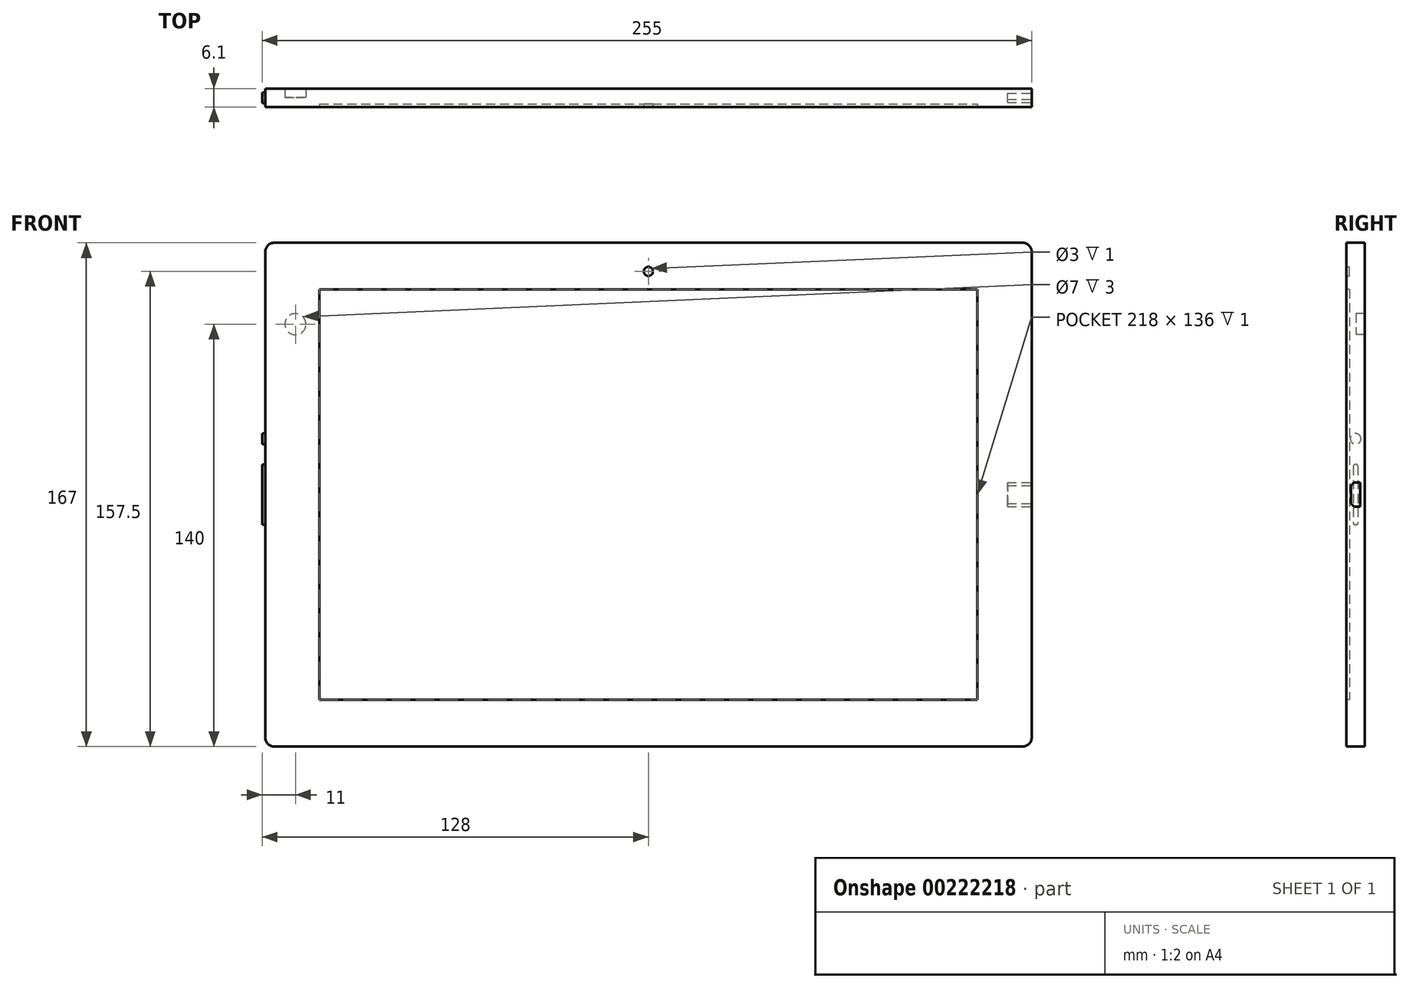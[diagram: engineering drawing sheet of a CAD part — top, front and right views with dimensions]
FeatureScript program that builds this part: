
annotation { "Feature Type Name" : "Feature", "Feature Type Description" : "" }
export const myFeature = defineFeature(function(context is Context, id is Id, definition is map)
    precondition{}
    {
        {
            var Q0;
            Q0=qCreatedBy(makeId("Front.planeOp"),FACE);
            var sketch = newSketch(context, id + "F0", { "sketchPlane" : qUnion([Q0])});
            skLineSegment(sketch, "E0.bottom", {"start": v(-127, 83.5) * mm, "end": v(127, 83.5) * mm});
            skLineSegment(sketch, "E0.top", {"start": v(-127, -83.5) * mm, "end": v(127, -83.5) * mm});
            skLineSegment(sketch, "E0.left", {"start": v(-127, 83.5) * mm, "end": v(-127, -83.5) * mm});
            skLineSegment(sketch, "E0.right", {"start": v(127, 83.5) * mm, "end": v(127, -83.5) * mm});
            skPoint(sketch, "E1", {"position": v(0, 83.5) * mm});
            skPoint(sketch, "E2", {"position": v(127, 0) * mm});
            skSolve(sketch);
        }
        {
            var Q0;
            Q0=makeQuery(id+"F0.imprint","IMPRINT",FACE,{"disambiguationData":[TD([[makeQuery(id+"F0.imprint","IMPRINT",EDGE,{"derivedFrom":sQuery(id+"F0.wireOp",EDGE,"E0.bottom")}),-1.0]])]});
            extrude(context, id + "F1", {"entities" : qUnion([Q0]), "endBound" : BoundingType.SYMMETRIC, "depth" : 6.1 * mm});
        }
        {
            var Q0;
            Q0=makeQuery(id+"F1.opExtrude","SWEPT_EDGE",EDGE,{"disambiguationData":[OSD([sQuery(id+"F0.wireOp",EDGE,"E0.bottom"),sQuery(id+"F0.wireOp",EDGE,"E0.right")])]});
            var Q1;
            Q1=makeQuery(id+"F1.opExtrude","SWEPT_EDGE",EDGE,{"disambiguationData":[OSD([sQuery(id+"F0.wireOp",EDGE,"E0.top"),sQuery(id+"F0.wireOp",EDGE,"E0.right")])]});
            var Q2;
            Q2=makeQuery(id+"F1.opExtrude","SWEPT_EDGE",EDGE,{"disambiguationData":[OSD([sQuery(id+"F0.wireOp",EDGE,"E0.top"),sQuery(id+"F0.wireOp",EDGE,"E0.left")])]});
            var Q3;
            Q3=makeQuery(id+"F1.opExtrude","SWEPT_EDGE",EDGE,{"disambiguationData":[OSD([sQuery(id+"F0.wireOp",EDGE,"E0.bottom"),sQuery(id+"F0.wireOp",EDGE,"E0.left")])]});
            fillet(context, id + "F2", {"entities" : qUnion([Q0, Q1, Q2, Q3]), "radius" : 3 * mm, "tangentPropagation" : true, "allowEdgeOverflow" : false});
        }
        {
            var Q0;
            Q0=makeQuery(id+"F1.opExtrude","CAP_FACE",FACE,{"disambiguationData":[OSD([sQuery(id+"F0.wireOp",EDGE,"E0.bottom"),sQuery(id+"F0.wireOp",EDGE,"E0.top"),sQuery(id+"F0.wireOp",EDGE,"E0.left"),sQuery(id+"F0.wireOp",EDGE,"E0.right")])],"isStart":false});
            var sketch = newSketch(context, id + "F3", { "sketchPlane" : qUnion([Q0])});
            skLineSegment(sketch, "E3.bottom", {"start": v(-109, 68) * mm, "end": v(109, 68) * mm});
            skLineSegment(sketch, "E3.top", {"start": v(-109, -68) * mm, "end": v(109, -68) * mm});
            skLineSegment(sketch, "E3.left", {"start": v(-109, 68) * mm, "end": v(-109, -68) * mm});
            skLineSegment(sketch, "E3.right", {"start": v(109, 68) * mm, "end": v(109, -68) * mm});
            skPoint(sketch, "E4", {"position": v(0, 68) * mm});
            skPoint(sketch, "E5", {"position": v(-109, 0) * mm});
            skPoint(sketch, "E6", {"position": v(0, 83.5) * mm});
            skPoint(sketch, "E7", {"position": v(-127, 0) * mm});
            skCircle(sketch, "E8", {"center": v(0, 74) * mm, "radius": 1.5 * mm});
            skSolve(sketch);
        }
        {
            var Q0;
            Q0=makeQuery(id+"F3.imprint","IMPRINT",FACE,{"disambiguationData":[TD([[makeQuery(id+"F3.imprint","IMPRINT",EDGE,{"derivedFrom":sQuery(id+"F3.wireOp",EDGE,"E3.bottom")}),-1.0]])]});
            var Q1;
            Q1=makeQuery(id+"F3.imprint","IMPRINT",FACE,{"disambiguationData":[TD([[makeQuery(id+"F3.imprint","IMPRINT",EDGE,{"derivedFrom":sQuery(id+"F3.wireOp",EDGE,"E8")}),1.0]])]});
            extrude(context, id + "F4", {"entities" : qUnion([Q0, Q1]), "operationType" : NewBodyOperationType.REMOVE, "oppositeDirection" : true, "depth" : 1 * mm});
        }
        {
            var Q0;
            Q0=makeQuery(id+"F4.boolean.opBoolean","COPY",FACE,{"derivedFrom":makeQuery(id+"F4.opExtrude","CAP_FACE",FACE,{"disambiguationData":[OSD([sQuery(id+"F3.wireOp",EDGE,"E3.bottom"),sQuery(id+"F3.wireOp",EDGE,"E3.top"),sQuery(id+"F3.wireOp",EDGE,"E3.left"),sQuery(id+"F3.wireOp",EDGE,"E3.right")])],"isStart":false})});
            var sketch = newSketch(context, id + "F5", { "sketchPlane" : qUnion([Q0])});
            skLineSegment(sketch, "E9.bottom", {"start": v(-109, 68) * mm, "end": v(109, 68) * mm});
            skLineSegment(sketch, "E9.top", {"start": v(-109, -68) * mm, "end": v(109, -68) * mm});
            skLineSegment(sketch, "E9.left", {"start": v(-109, 68) * mm, "end": v(-109, -68) * mm});
            skLineSegment(sketch, "E9.right", {"start": v(109, 68) * mm, "end": v(109, -68) * mm});
            skCircle(sketch, "E10.0.0", {"center": v(0, 74) * mm, "radius": 1.5 * mm});
            skSolve(sketch);
        }
        {
            var Q0;
            Q0=makeQuery(id+"F5.imprint","IMPRINT",FACE,{"disambiguationData":[TD([[makeQuery(id+"F5.imprint","IMPRINT",EDGE,{"derivedFrom":sQuery(id+"F5.wireOp",EDGE,"E9.bottom")}),-1.0]])]});
            var Q1;
            Q1=makeQuery(id+"F5.imprint","IMPRINT",FACE,{"disambiguationData":[TD([[makeQuery(id+"F5.imprint","IMPRINT",EDGE,{"derivedFrom":sQuery(id+"F5.wireOp",EDGE,"E10.0.0")}),1.0]])]});
            var Q2;
            Q2=makeQuery(id+"F1.opExtrude","CAP_FACE",FACE,{"disambiguationData":[OSD([sQuery(id+"F0.wireOp",EDGE,"E0.bottom"),sQuery(id+"F0.wireOp",EDGE,"E0.top"),sQuery(id+"F0.wireOp",EDGE,"E0.left"),sQuery(id+"F0.wireOp",EDGE,"E0.right")])],"isStart":false});
            extrude(context, id + "F6", {"entities" : qUnion([Q0, Q1]), "endBound" : BoundingType.UP_TO_SURFACE, "endBoundEntityFace" : qUnion([Q2]), "depth" : 25 * mm});
        }
        {
            var Q0;
            Q0=makeQuery(id+"F1.opExtrude","CAP_FACE",FACE,{"disambiguationData":[OSD([sQuery(id+"F0.wireOp",EDGE,"E0.bottom"),sQuery(id+"F0.wireOp",EDGE,"E0.top"),sQuery(id+"F0.wireOp",EDGE,"E0.left"),sQuery(id+"F0.wireOp",EDGE,"E0.right")])],"isStart":true});
            var sketch = newSketch(context, id + "F7", { "sketchPlane" : qUnion([Q0])});
            skCircle(sketch, "E11", {"center": v(117, 56.5) * mm, "radius": 3.5 * mm});
            skSolve(sketch);
        }
        {
            var Q0;
            Q0=makeQuery(id+"F7.imprint","IMPRINT",FACE,{"disambiguationData":[TD([[makeQuery(id+"F7.imprint","IMPRINT",EDGE,{"derivedFrom":sQuery(id+"F7.wireOp",EDGE,"E11")}),1.0]])]});
            extrude(context, id + "F8", {"entities" : qUnion([Q0]), "operationType" : NewBodyOperationType.REMOVE, "oppositeDirection" : true, "depth" : 3 * mm});
        }
        {
            var Q0;
            Q0=makeQuery(id+"F8.boolean.opBoolean","COPY",FACE,{"derivedFrom":makeQuery(id+"F8.opExtrude","CAP_FACE",FACE,{"disambiguationData":[OSD([sQuery(id+"F7.wireOp",EDGE,"E11")])],"isStart":false})});
            var sketch = newSketch(context, id + "F9", { "sketchPlane" : qUnion([Q0])});
            skCircle(sketch, "E12", {"center": v(117, 56.5) * mm, "radius": 3.5 * mm});
            skSolve(sketch);
        }
        {
            var Q0;
            Q0=makeQuery(id+"F9.imprint","IMPRINT",FACE,{"disambiguationData":[TD([[makeQuery(id+"F9.imprint","IMPRINT",EDGE,{"derivedFrom":sQuery(id+"F9.wireOp",EDGE,"E12")}),1.0]])]});
            extrude(context, id + "F10", {"entities" : qUnion([Q0]), "depth" : 3 * mm});
        }
        {
            var Q0;
            Q0=makeQuery(id+"F1.opExtrude","SWEPT_FACE",FACE,{"disambiguationData":[OSD([sQuery(id+"F0.wireOp",EDGE,"E0.left")])]});
            var sketch = newSketch(context, id + "F11", { "sketchPlane" : qUnion([Q0])});
            skCircle(sketch, "E13", {"center": v(0, 18.5) * mm, "radius": 1.75 * mm});
            skLineSegment(sketch, "E14.bottom", {"start": v(-0.15, 10) * mm, "end": v(0.15, 10) * mm});
            skLineSegment(sketch, "E14.top", {"start": v(-0.15, -10) * mm, "end": v(0.15, -10) * mm});
            skLineSegment(sketch, "E14.left", {"start": v(-0.75, 9.4) * mm, "end": v(-0.75, -9.4) * mm});
            skLineSegment(sketch, "E14.right", {"start": v(0.75, 9.4) * mm, "end": v(0.75, -9.4) * mm});
            skPoint(sketch, "E15", {"position": v(0, 10) * mm});
            skPoint(sketch, "E16", {"position": v(-0.75, 0) * mm});
            skPoint(sketch, "E17.visualSharp", {"position": v(-0.75, 10) * mm});
            skArc(sketch, "E17.filletArc", {"start": v(-0.15, 10) * mm, "mid": v(-0.57, 9.82) * mm, "end": v(-0.75, 9.4) * mm});
            skPoint(sketch, "E18.visualSharp", {"position": v(0.75, 10) * mm});
            skArc(sketch, "E18.filletArc", {"start": v(0.75, 9.4) * mm, "mid": v(0.57, 9.82) * mm, "end": v(0.15, 10) * mm});
            skPoint(sketch, "E19.visualSharp", {"position": v(0.75, -10) * mm});
            skArc(sketch, "E19.filletArc", {"start": v(0.15, -10) * mm, "mid": v(0.57, -9.82) * mm, "end": v(0.75, -9.4) * mm});
            skPoint(sketch, "E20.visualSharp", {"position": v(-0.75, -10) * mm});
            skArc(sketch, "E20.filletArc", {"start": v(-0.75, -9.4) * mm, "mid": v(-0.57, -9.82) * mm, "end": v(-0.15, -10) * mm});
            skSolve(sketch);
        }
        {
            var Q0;
            Q0=makeQuery(id+"F11.imprint","IMPRINT",FACE,{"disambiguationData":[TD([[makeQuery(id+"F11.imprint","IMPRINT",EDGE,{"derivedFrom":sQuery(id+"F11.wireOp",EDGE,"E13")}),1.0]])]});
            var Q1;
            Q1=makeQuery(id+"F11.imprint","IMPRINT",FACE,{"disambiguationData":[TD([[makeQuery(id+"F11.imprint","IMPRINT",EDGE,{"derivedFrom":sQuery(id+"F11.wireOp",EDGE,"E14.bottom")}),-1.0]])]});
            extrude(context, id + "F12", {"entities" : qUnion([Q0, Q1]), "operationType" : NewBodyOperationType.ADD, "depth" : 1 * mm});
        }
        {
            var Q0;
            Q0=makeQuery(id+"F1.opExtrude","SWEPT_FACE",FACE,{"disambiguationData":[OSD([sQuery(id+"F0.wireOp",EDGE,"E0.right")])]});
            var sketch = newSketch(context, id + "F13", { "sketchPlane" : qUnion([Q0])});
            skLineSegment(sketch, "E21", {"start": v(1.5, 4) * mm, "end": v(1.5, -4) * mm});
            skLineSegment(sketch, "E22", {"start": v(1.5, -4) * mm, "end": v(-0.5, -4) * mm});
            skLineSegment(sketch, "E23", {"start": v(-0.5, -4) * mm, "end": v(-1.5, -3) * mm});
            skLineSegment(sketch, "E24", {"start": v(-1.5, -3) * mm, "end": v(-1.5, 3) * mm});
            skLineSegment(sketch, "E25", {"start": v(-1.5, 3) * mm, "end": v(-0.5, 4) * mm});
            skLineSegment(sketch, "E26", {"start": v(-0.5, 4) * mm, "end": v(1.5, 4) * mm});
            skLineSegment(sketch, "E27", {"start": v(-1.5, 0) * mm, "end": v(1.5, 0) * mm, "construction": true});
            skPoint(sketch, "E28", {"position": v(0, 0) * mm});
            skSolve(sketch);
        }
        {
            var Q0;
            Q0=makeQuery(id+"F13.imprint","IMPRINT",FACE,{"disambiguationData":[TD([[makeQuery(id+"F13.imprint","IMPRINT",EDGE,{"derivedFrom":sQuery(id+"F13.wireOp",EDGE,"E21")}),-1.0]])]});
            extrude(context, id + "F14", {"entities" : qUnion([Q0]), "operationType" : NewBodyOperationType.REMOVE, "oppositeDirection" : true, "depth" : 8 * mm});
        }
    });
